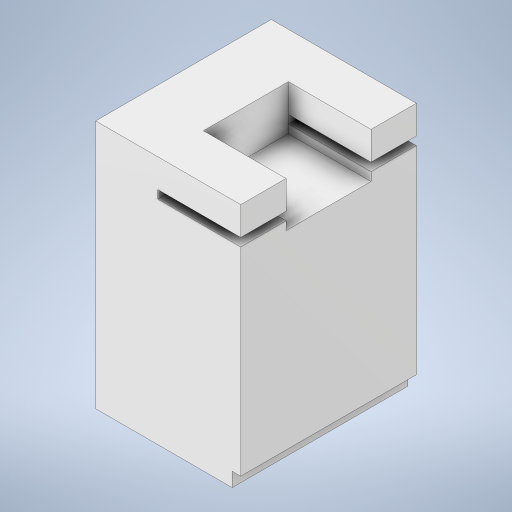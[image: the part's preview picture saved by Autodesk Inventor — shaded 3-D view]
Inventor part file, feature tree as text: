
AUTODESK INVENTOR PART (.ipt)
format: ipt  version: 2023 (Build 270158000, 158)  size: 435,712 bytes
history: native  units: in
note: dims shown in document units (in); Inventor stores cm internally (conversion verified against a paired STEP export)
features: extrude x14, sketch x10, fillet x2, shell x1, projected_geometry x1
ambient origin geometry x8: Origin, YZ Plane, XZ Plane, XY Plane, X Axis, Y Axis, Z Axis, Center Point
bodies: Body1 (feature_tree)
feature tree (28):
  extrude  "Extrusion4"  Depth=4.5in
  extrude  "Extrusion7"  Depth=2.4in
  extrude  "Extrusion8"  Depth=1.125in
  fillet  "Fillet3"  Radius=2.25in
  extrude  "Extrusion11"  Depth=0.075in
  extrude  "Extrusion12"  Depth=0.25in
  fillet  "Fillet4"  Radius=0.125in
  extrude  "Extrusion13"  Depth=0.125in
  shell  "Shell4"  Thickness=1.6125in
  extrude  "Extrusion14"  Depth=0.25in
  extrude  "Extrusion15"  Depth=1.0in TaperAngle=0.0deg
  extrude  "Extrusion16"  Depth=0.1in
  extrude  "Extrusion17"  Depth=0.4in
  extrude  "Extrusion18"  Depth=0.4in
  extrude  "Extrusion19"  Depth=0.4in TaperAngle=0.0deg
  extrude  "Extrusion20"  Depth=0.4in
  extrude  "Extrusion21"  Depth=0.4in
  sketch  "Sketch1"  dims[d0=7.0in d1=4.5in]
  sketch  "Sketch6"  dims[d32=1.0in d33=0.0in d34=2.4in]
  sketch  "Sketch7"  dims[d35=1.275in d36=1.125in d37=2.25in]
  sketch  "Sketch8"  dims[d38=0.075in d39=0.075in]
  sketch  "Sketch9"  dims[d41=1.6125in d42=0.25in d62=0.125in d63=0.0in]
  sketch  "Sketch10"  dims[d64=0.85in d65=0.0in d75=0.125in d82=1.6125in]
  projected_geometry  "Projected Loop1"
  sketch  "Sketch11"  dims[d83=0.375in d84=0.25in]
  sketch  "Sketch12"  dims[d85=0.5625in d86=1.0in d87=0.0in]
  sketch  "Sketch13"  dims[d88=0.0665in d89=0.0in d90=0.1in]
  sketch  "Sketch14"  dims[d91=0.0625in d92=0.0625in d93=0.0625in d94=0.1in d95=0.0in d96=0.2in d97=0.155in d98=0.155in d99=0.155in d100=0.155in d101=0.155in d102=0.155in d103=0.1in d104=0.1in d105=0.1in d106=0.1in d107=0.1in d108=0.1in d109=0.1in d110=0.1in d111=0.1in d112=0.1in d113=3.5in d114=3.5in d115=0.25in d116=0.0in d117=3.0in d118=0.0in d119=1.4in d120=0.25in d121=0.55in d122=0.073in d123=0.4in d124=0.0in d125=7.0in d126=0.0in d127=0.0075in d128=7.0in d129=0.0in d130=0.0075in d131=7.0in d132=0.0in d133=0.075in d134=0.75in d135=0.0in d136=0.4in d137=0.0in]
